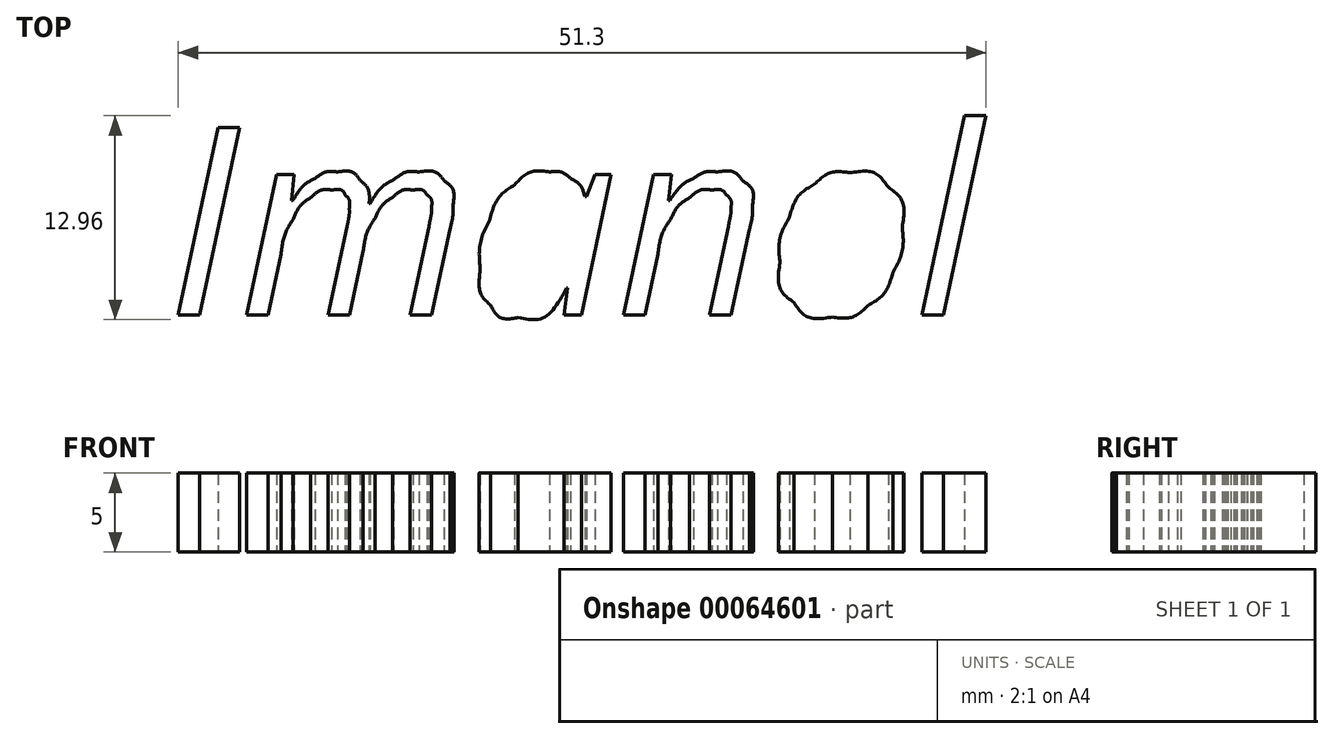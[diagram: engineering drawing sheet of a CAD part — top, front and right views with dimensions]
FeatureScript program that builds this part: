
annotation { "Feature Type Name" : "Feature", "Feature Type Description" : "" }
export const myFeature = defineFeature(function(context is Context, id is Id, definition is map)
    precondition{}
    {
        {
            var Q0;
            Q0=qCreatedBy(makeId("Top.planeOp"),FACE);
            var sketch = newSketch(context, id + "F0", { "sketchPlane" : qUnion([Q0])});
            skLineSegment(sketch, "E0.0.0", {"start": v(-62.43, 33.25) * mm, "end": v(-64.96, 21.35) * mm});
            skLineSegment(sketch, "E0.0.1", {"start": v(-64.96, 21.35) * mm, "end": v(-63.6, 21.35) * mm});
            skLineSegment(sketch, "E0.0.2", {"start": v(-63.6, 21.35) * mm, "end": v(-61.06, 33.25) * mm});
            skLineSegment(sketch, "E0.0.3", {"start": v(-61.06, 33.25) * mm, "end": v(-62.43, 33.25) * mm});
            skLineSegment(sketch, "E1.0.0", {"start": v(-54.24, 26.98) * mm, "end": v(-55.45, 21.35) * mm});
            skLineSegment(sketch, "E1.0.1", {"start": v(-55.45, 21.35) * mm, "end": v(-54.08, 21.35) * mm});
            skLineSegment(sketch, "E1.0.2", {"start": v(-54.08, 21.35) * mm, "end": v(-53.21, 25.42) * mm});
            skFitSpline(sketch, "E1.0.3", {"points": [v(-53.21, 25.42) * mm, v(-52.96, 26.6) * mm, v(-52.47, 27.47) * mm]});
            skFitSpline(sketch, "E1.0.4", {"points": [v(-52.47, 27.47) * mm, v(-51.99, 28.34) * mm, v(-51.35, 28.8) * mm]});
            skFitSpline(sketch, "E1.0.5", {"points": [v(-51.35, 28.8) * mm, v(-50.7, 29.28) * mm, v(-50.04, 29.28) * mm]});
            skFitSpline(sketch, "E1.0.6", {"points": [v(-50.04, 29.28) * mm, v(-49.44, 29.28) * mm, v(-49.16, 28.98) * mm]});
            skFitSpline(sketch, "E1.0.7", {"points": [v(-49.16, 28.98) * mm, v(-48.88, 28.67) * mm, v(-48.88, 28.17) * mm]});
            skFitSpline(sketch, "E1.0.8", {"points": [v(-48.88, 28.17) * mm, v(-48.88, 27.83) * mm, v(-49.04, 26.98) * mm]});
            skLineSegment(sketch, "E1.0.9", {"start": v(-49.04, 26.98) * mm, "end": v(-50.25, 21.35) * mm});
            skLineSegment(sketch, "E1.0.10", {"start": v(-50.25, 21.35) * mm, "end": v(-48.86, 21.35) * mm});
            skLineSegment(sketch, "E1.0.11", {"start": v(-48.86, 21.35) * mm, "end": v(-47.7, 26.82) * mm});
            skFitSpline(sketch, "E1.0.12", {"points": [v(-47.7, 26.82) * mm, v(-47.51, 27.71) * mm, v(-47.51, 28.26) * mm]});
            skFitSpline(sketch, "E1.0.13", {"points": [v(-47.51, 28.26) * mm, v(-47.51, 29.32) * mm, v(-48.08, 29.88) * mm]});
            skFitSpline(sketch, "E1.0.14", {"points": [v(-48.08, 29.88) * mm, v(-48.64, 30.43) * mm, v(-49.68, 30.43) * mm]});
            skFitSpline(sketch, "E1.0.15", {"points": [v(-49.68, 30.43) * mm, v(-50.48, 30.43) * mm, v(-51.27, 29.94) * mm]});
            skFitSpline(sketch, "E1.0.16", {"points": [v(-51.27, 29.94) * mm, v(-52.06, 29.44) * mm, v(-52.76, 28.43) * mm]});
            skLineSegment(sketch, "E1.0.17", {"start": v(-52.76, 28.43) * mm, "end": v(-52.83, 28.43) * mm});
            skFitSpline(sketch, "E1.0.18", {"points": [v(-52.83, 28.43) * mm, v(-52.92, 29.37) * mm, v(-53.41, 29.9) * mm]});
            skFitSpline(sketch, "E1.0.19", {"points": [v(-53.41, 29.9) * mm, v(-53.9, 30.43) * mm, v(-54.83, 30.43) * mm]});
            skFitSpline(sketch, "E1.0.20", {"points": [v(-54.83, 30.43) * mm, v(-55.58, 30.43) * mm, v(-56.28, 30) * mm]});
            skFitSpline(sketch, "E1.0.21", {"points": [v(-56.28, 30) * mm, v(-56.99, 29.58) * mm, v(-57.7, 28.62) * mm]});
            skLineSegment(sketch, "E1.0.22", {"start": v(-57.7, 28.62) * mm, "end": v(-57.78, 28.62) * mm});
            skLineSegment(sketch, "E1.0.23", {"start": v(-57.78, 28.62) * mm, "end": v(-57.6, 30.27) * mm});
            skLineSegment(sketch, "E1.0.24", {"start": v(-57.6, 30.27) * mm, "end": v(-58.73, 30.27) * mm});
            skLineSegment(sketch, "E1.0.25", {"start": v(-58.73, 30.27) * mm, "end": v(-60.63, 21.35) * mm});
            skLineSegment(sketch, "E1.0.26", {"start": v(-60.63, 21.35) * mm, "end": v(-59.27, 21.35) * mm});
            skLineSegment(sketch, "E1.0.27", {"start": v(-59.27, 21.35) * mm, "end": v(-58.44, 25.21) * mm});
            skFitSpline(sketch, "E1.0.28", {"points": [v(-58.44, 25.21) * mm, v(-58.17, 26.5) * mm, v(-57.68, 27.4) * mm]});
            skFitSpline(sketch, "E1.0.29", {"points": [v(-57.68, 27.4) * mm, v(-57.2, 28.3) * mm, v(-56.54, 28.8) * mm]});
            skFitSpline(sketch, "E1.0.30", {"points": [v(-56.54, 28.8) * mm, v(-55.9, 29.28) * mm, v(-55.21, 29.28) * mm]});
            skFitSpline(sketch, "E1.0.31", {"points": [v(-55.21, 29.28) * mm, v(-54.6, 29.28) * mm, v(-54.35, 28.96) * mm]});
            skFitSpline(sketch, "E1.0.32", {"points": [v(-54.35, 28.96) * mm, v(-54.1, 28.65) * mm, v(-54.1, 28.08) * mm]});
            skFitSpline(sketch, "E1.0.33", {"points": [v(-54.1, 28.08) * mm, v(-54.1, 27.74) * mm, v(-54.24, 26.98) * mm]});
            skFitSpline(sketch, "E2.0.0", {"points": [v(-40.04, 30.03) * mm, v(-40.63, 30.43) * mm, v(-41.38, 30.43) * mm]});
            skFitSpline(sketch, "E2.0.1", {"points": [v(-41.38, 30.43) * mm, v(-42.6, 30.43) * mm, v(-43.6, 29.6) * mm]});
            skFitSpline(sketch, "E2.0.2", {"points": [v(-43.6, 29.6) * mm, v(-44.63, 28.78) * mm, v(-45.2, 27.34) * mm]});
            skFitSpline(sketch, "E2.0.3", {"points": [v(-45.2, 27.34) * mm, v(-45.78, 25.89) * mm, v(-45.78, 24.2) * mm]});
            skFitSpline(sketch, "E2.0.4", {"points": [v(-45.78, 24.2) * mm, v(-45.78, 22.8) * mm, v(-45.14, 21.99) * mm]});
            skFitSpline(sketch, "E2.0.5", {"points": [v(-45.14, 21.99) * mm, v(-44.5, 21.18) * mm, v(-43.36, 21.18) * mm]});
            skFitSpline(sketch, "E2.0.6", {"points": [v(-43.36, 21.18) * mm, v(-41.75, 21.18) * mm, v(-40.3, 23.05) * mm]});
            skLineSegment(sketch, "E2.0.7", {"start": v(-40.3, 23.05) * mm, "end": v(-40.23, 23.05) * mm});
            skLineSegment(sketch, "E2.0.8", {"start": v(-40.23, 23.05) * mm, "end": v(-40.44, 21.35) * mm});
            skLineSegment(sketch, "E2.0.9", {"start": v(-40.44, 21.35) * mm, "end": v(-39.36, 21.35) * mm});
            skLineSegment(sketch, "E2.0.10", {"start": v(-39.36, 21.35) * mm, "end": v(-37.46, 30.27) * mm});
            skLineSegment(sketch, "E2.0.11", {"start": v(-37.46, 30.27) * mm, "end": v(-38.5, 30.27) * mm});
            skLineSegment(sketch, "E2.0.12", {"start": v(-38.5, 30.27) * mm, "end": v(-39.04, 28.87) * mm});
            skLineSegment(sketch, "E2.0.13", {"start": v(-39.04, 28.87) * mm, "end": v(-39.13, 28.87) * mm});
            skFitSpline(sketch, "E2.0.14", {"points": [v(-39.13, 28.87) * mm, v(-39.46, 29.62) * mm, v(-40.04, 30.03) * mm]});
            skLineSegment(sketch, "E3.0.0", {"start": v(-30.02, 26.98) * mm, "end": v(-31.23, 21.35) * mm});
            skLineSegment(sketch, "E3.0.1", {"start": v(-31.23, 21.35) * mm, "end": v(-29.85, 21.35) * mm});
            skLineSegment(sketch, "E3.0.2", {"start": v(-29.85, 21.35) * mm, "end": v(-28.68, 26.82) * mm});
            skFitSpline(sketch, "E3.0.3", {"points": [v(-28.68, 26.82) * mm, v(-28.5, 27.64) * mm, v(-28.5, 28.28) * mm]});
            skFitSpline(sketch, "E3.0.4", {"points": [v(-28.5, 28.28) * mm, v(-28.5, 29.3) * mm, v(-29.1, 29.86) * mm]});
            skFitSpline(sketch, "E3.0.5", {"points": [v(-29.1, 29.86) * mm, v(-29.7, 30.43) * mm, v(-30.72, 30.43) * mm]});
            skFitSpline(sketch, "E3.0.6", {"points": [v(-30.72, 30.43) * mm, v(-31.5, 30.43) * mm, v(-32.23, 30.02) * mm]});
            skFitSpline(sketch, "E3.0.7", {"points": [v(-32.23, 30.02) * mm, v(-32.96, 29.6) * mm, v(-33.74, 28.62) * mm]});
            skLineSegment(sketch, "E3.0.8", {"start": v(-33.74, 28.62) * mm, "end": v(-33.83, 28.62) * mm});
            skLineSegment(sketch, "E3.0.9", {"start": v(-33.83, 28.62) * mm, "end": v(-33.65, 30.27) * mm});
            skLineSegment(sketch, "E3.0.10", {"start": v(-33.65, 30.27) * mm, "end": v(-34.78, 30.27) * mm});
            skLineSegment(sketch, "E3.0.11", {"start": v(-34.78, 30.27) * mm, "end": v(-36.68, 21.35) * mm});
            skLineSegment(sketch, "E3.0.12", {"start": v(-36.68, 21.35) * mm, "end": v(-35.32, 21.35) * mm});
            skLineSegment(sketch, "E3.0.13", {"start": v(-35.32, 21.35) * mm, "end": v(-34.5, 25.21) * mm});
            skFitSpline(sketch, "E3.0.14", {"points": [v(-34.5, 25.21) * mm, v(-34.22, 26.5) * mm, v(-33.7, 27.4) * mm]});
            skFitSpline(sketch, "E3.0.15", {"points": [v(-33.7, 27.4) * mm, v(-33.17, 28.3) * mm, v(-32.49, 28.8) * mm]});
            skFitSpline(sketch, "E3.0.16", {"points": [v(-32.49, 28.8) * mm, v(-31.8, 29.28) * mm, v(-31.07, 29.28) * mm]});
            skFitSpline(sketch, "E3.0.17", {"points": [v(-31.07, 29.28) * mm, v(-30.44, 29.28) * mm, v(-30.15, 28.97) * mm]});
            skFitSpline(sketch, "E3.0.18", {"points": [v(-30.15, 28.97) * mm, v(-29.86, 28.66) * mm, v(-29.86, 28.15) * mm]});
            skFitSpline(sketch, "E3.0.19", {"points": [v(-29.86, 28.15) * mm, v(-29.86, 27.83) * mm, v(-30.02, 26.98) * mm]});
            skFitSpline(sketch, "E4.0.0", {"points": [v(-19.87, 29.47) * mm, v(-20.76, 30.38) * mm, v(-22.31, 30.38) * mm]});
            skFitSpline(sketch, "E4.0.1", {"points": [v(-22.31, 30.38) * mm, v(-23.54, 30.38) * mm, v(-24.55, 29.65) * mm]});
            skFitSpline(sketch, "E4.0.2", {"points": [v(-24.55, 29.65) * mm, v(-25.55, 28.92) * mm, v(-26.15, 27.56) * mm]});
            skFitSpline(sketch, "E4.0.3", {"points": [v(-26.15, 27.56) * mm, v(-26.74, 26.2) * mm, v(-26.74, 24.65) * mm]});
            skFitSpline(sketch, "E4.0.4", {"points": [v(-26.74, 24.65) * mm, v(-26.74, 23.06) * mm, v(-25.86, 22.14) * mm]});
            skFitSpline(sketch, "E4.0.5", {"points": [v(-25.86, 22.14) * mm, v(-24.97, 21.22) * mm, v(-23.4, 21.22) * mm]});
            skFitSpline(sketch, "E4.0.6", {"points": [v(-23.4, 21.22) * mm, v(-22.15, 21.22) * mm, v(-21.14, 21.96) * mm]});
            skFitSpline(sketch, "E4.0.7", {"points": [v(-21.14, 21.96) * mm, v(-20.14, 22.7) * mm, v(-19.56, 24.06) * mm]});
            skFitSpline(sketch, "E4.0.8", {"points": [v(-19.56, 24.06) * mm, v(-18.97, 25.42) * mm, v(-18.97, 26.95) * mm]});
            skFitSpline(sketch, "E4.0.9", {"points": [v(-18.97, 26.95) * mm, v(-18.97, 28.55) * mm, v(-19.87, 29.47) * mm]});
            skLineSegment(sketch, "E5.0.0", {"start": v(-17.73, 21.35) * mm, "end": v(-16.36, 21.35) * mm});
            skLineSegment(sketch, "E5.0.1", {"start": v(-16.36, 21.35) * mm, "end": v(-13.66, 34.01) * mm});
            skLineSegment(sketch, "E5.0.2", {"start": v(-13.66, 34.01) * mm, "end": v(-15.02, 34.01) * mm});
            skLineSegment(sketch, "E5.0.3", {"start": v(-15.02, 34.01) * mm, "end": v(-17.73, 21.35) * mm});
            skSolve(sketch);
        }
        {
            var Q0;
            Q0 = qSketchRegion(id + "F0", true);
            extrude(context, id + "F1", {"entities" : qUnion([Q0]), "depth" : 5 * mm});
        }
    });
